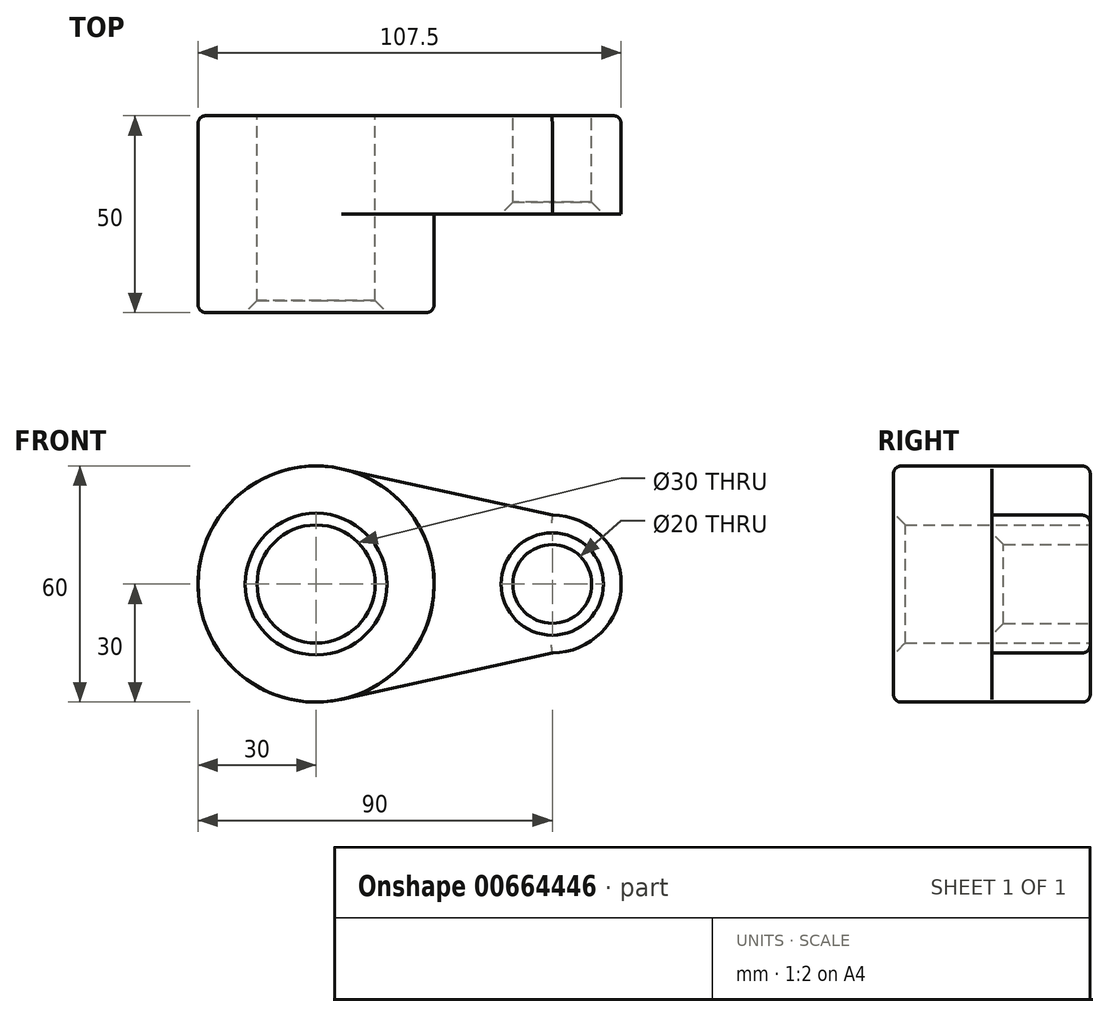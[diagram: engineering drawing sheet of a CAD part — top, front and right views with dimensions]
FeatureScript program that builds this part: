
annotation { "Feature Type Name" : "Feature", "Feature Type Description" : "" }
export const myFeature = defineFeature(function(context is Context, id is Id, definition is map)
    precondition{}
    {
        {
            var Q0;
            Q0=qCreatedBy(makeId("Front.planeOp"),FACE);
            var sketch = newSketch(context, id + "F0", { "sketchPlane" : qUnion([Q0])});
            skCircle(sketch, "E0", {"center": v(0, 0) * mm, "radius": 30 * mm});
            skCircle(sketch, "E1", {"center": v(60, 0) * mm, "radius": 17.5 * mm});
            skLineSegment(sketch, "E2", {"start": v(6.45, 29.3) * mm, "end": v(60, 17.5) * mm});
            skCircle(sketch, "E3", {"center": v(0, 0) * mm, "radius": 15 * mm});
            skCircle(sketch, "E4", {"center": v(60, 0) * mm, "radius": 10 * mm});
            skLineSegment(sketch, "E5", {"start": v(6.45, -29.3) * mm, "end": v(60, -17.5) * mm});
            skSolve(sketch);
        }
        {
            var Q0;
            Q0=qSketchRegion(id+"F0",true);
            extrude(context, id + "F1", {"entities" : qUnion([Q0]), "depth" : 25 * mm});
        }
        {
            var Q0;
            Q0=makeQuery(id+"F0.imprint","IMPRINT",FACE,{"disambiguationData":[TD([[makeQuery(id+"F0.imprint","IMPRINT",EDGE,{"derivedFrom":sQuery(id+"F0.wireOp",EDGE,"E3")}),-1.0]])]});
            extrude(context, id + "F2", {"entities" : qUnion([Q0]), "operationType" : NewBodyOperationType.ADD, "depth" : 50 * mm});
        }
        {
            var Q0;
            Q0=makeQuery(id+"F1.opExtrude","CAP_EDGE",EDGE,{"disambiguationData":[OSD([sQuery(id+"F0.wireOp",EDGE,"E5")])],"isStart":true});
            var Q1;
            Q1=makeQuery(id+"F2.opExtrude","CAP_EDGE",EDGE,{"disambiguationData":[OSD([sQuery(id+"F0.wireOp",EDGE,"E0")])],"isStart":false});
            var Q2;
            Q2=makeQuery(id+"F1.opExtrude","CAP_EDGE",EDGE,{"disambiguationData":[OSD([sQuery(id+"F0.wireOp",EDGE,"E1")])],"isStart":true});
            var Q3;
            Q3=makeQuery(id+"F1.opExtrude","CAP_EDGE",EDGE,{"disambiguationData":[OSD([sQuery(id+"F0.wireOp",EDGE,"E0")])],"isStart":true});
            var Q4;
            Q4=makeQuery(id+"F1.opExtrude","CAP_EDGE",EDGE,{"disambiguationData":[OSD([sQuery(id+"F0.wireOp",EDGE,"E2")])],"isStart":true});
            fillet(context, id + "F3", {"entities" : qUnion([Q0, Q1, Q2, Q3, Q4]), "radius" : 2 * mm, "tangentPropagation" : true, "allowEdgeOverflow" : false});
        }
        {
            var Q0;
            Q0=makeQuery(id+"F2.opExtrude","CAP_EDGE",EDGE,{"disambiguationData":[OSD([sQuery(id+"F0.wireOp",EDGE,"E3")])],"isStart":false});
            var Q1;
            Q1=makeQuery(id+"F1.opExtrude","CAP_EDGE",EDGE,{"disambiguationData":[OSD([sQuery(id+"F0.wireOp",EDGE,"E4")])],"isStart":false});
            chamfer(context, id + "F4", {"entities" : qUnion([Q0, Q1]), "width" : 3 * mm, "tangentPropagation" : true});
        }
    });
